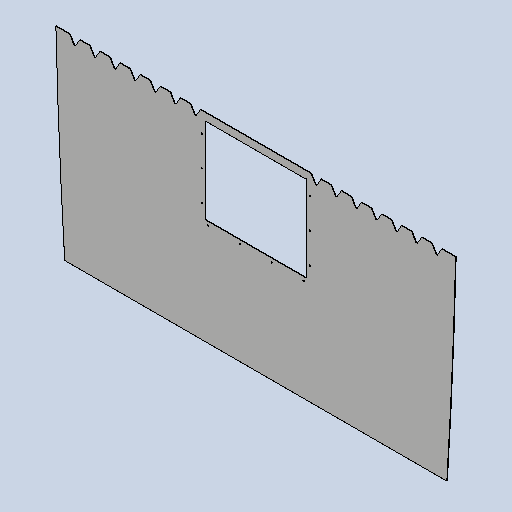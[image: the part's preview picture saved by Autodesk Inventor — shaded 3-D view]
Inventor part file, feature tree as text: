
AUTODESK INVENTOR PART (.ipt)
format: ipt  version: 2025 (Build 290162010, 162A)  size: 283,136 bytes
history: native  units: mm
features: sketch x3, other x2, sheet_metal_op x1, extrude x1, pattern_linear x1, hole x1, mirror x1, projected_geometry x1
ambient origin geometry x8: Origin, YZ Plane, XZ Plane, XY Plane, X Axis, Y Axis, Z Axis, Center Point
bodies: Solid1 (feature_tree)
feature tree (11):
  sheet_metal_op  "Face1"
  extrude  "Extrusion1"  Depth=790.0mm
  pattern_linear  "Rectangular Pattern1"  Count1=20  [1 undecoded]
  sketch  "Sketch7"  dims[d19=370.0mm d23=900.0mm d34=30.0mm d35=5.0mm d36=40.0mm d38=0.0mm d39=0.0mm d40=70.0mm d42=80.0mm d43=30.0mm d44=20.0mm d45=15.0mm d46=240.0mm d47=10.0mm d48=15.0mm d49=190.0mm d50=126.666667mm d51=5.1mm d52=6.0mm d53=4.0mm d54=2.0mm d55=90.0deg d56=2.0mm d57=20.594885mm d58=760.0mm d59=790.0mm d60=795.0mm d61=20475.0mm]
  hole  "Hole1"  [1 undecoded]
  mirror  "Mirror1"
  sketch  "Sketch1"  dims[d0=513.0mm d2=790.0mm]
  other  "Plate1"
  sketch  "Sketch5"  dims[d3=2.0mm d6=200.0mm]
  projected_geometry  "Projected Loop1"
  other  "Definition1"
note: 2 required parameter values undecoded (feature->parameter linkage not recoverable at this tier; creation-order binding heuristic only, values carry confidence <= 0.55)
